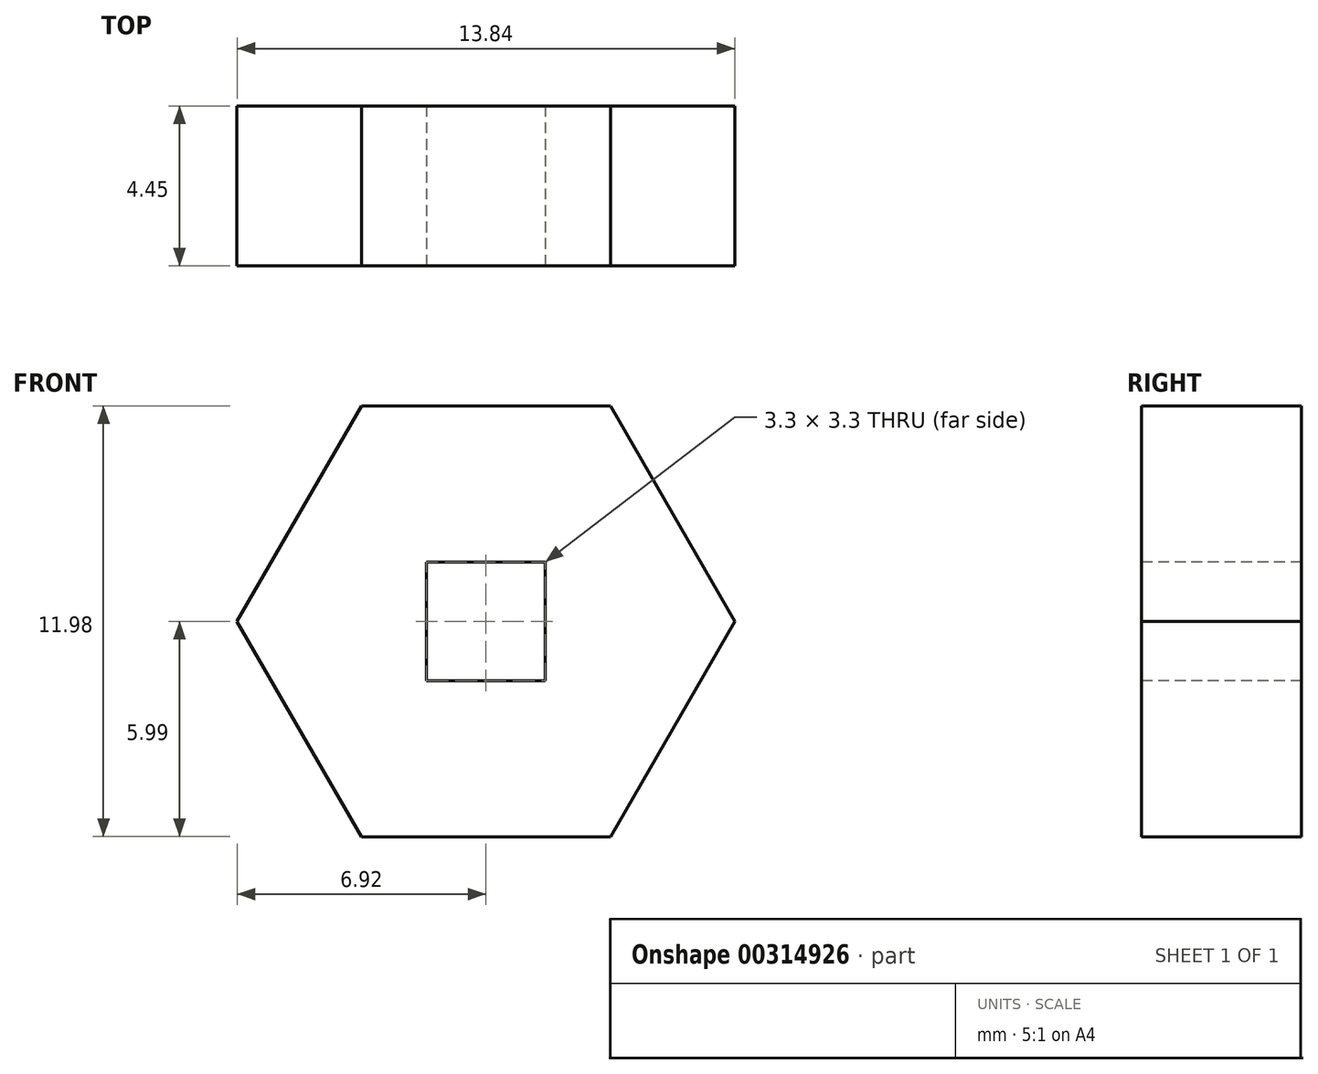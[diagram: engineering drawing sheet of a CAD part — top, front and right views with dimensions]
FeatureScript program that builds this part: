
annotation { "Feature Type Name" : "Feature", "Feature Type Description" : "" }
export const myFeature = defineFeature(function(context is Context, id is Id, definition is map)
    precondition{}
    {
        {
            var Q0;
            Q0=qCreatedBy(makeId("Front.planeOp"),FACE);
            var sketch = newSketch(context, id + "F0", { "sketchPlane" : qUnion([Q0])});
            skCircle(sketch, "E0.cCircle", {"center": v(0, 0) * mm, "radius": 6 * mm, "construction": true});
            skLineSegment(sketch, "E0.0", {"start": v(-3.46, 6) * mm, "end": v(3.46, 6) * mm});
            skLineSegment(sketch, "E0.1", {"start": v(3.46, 6) * mm, "end": v(6.92, 0) * mm});
            skLineSegment(sketch, "E0.2", {"start": v(6.92, 0) * mm, "end": v(3.46, -6) * mm});
            skLineSegment(sketch, "E0.3", {"start": v(3.46, -6) * mm, "end": v(-3.46, -6) * mm});
            skLineSegment(sketch, "E0.4", {"start": v(-3.46, -6) * mm, "end": v(-6.92, 0) * mm});
            skLineSegment(sketch, "E0.5", {"start": v(-6.92, 0) * mm, "end": v(-3.46, 6) * mm});
            skPoint(sketch, "E0.0.midPoint", {"position": v(0, 6) * mm});
            skSolve(sketch);
        }
        {
            var Q0;
            Q0=makeQuery(id+"F0.imprint","IMPRINT",FACE,{"disambiguationData":[TD([[makeQuery(id+"F0.imprint","IMPRINT",EDGE,{"derivedFrom":sQuery(id+"F0.wireOp",EDGE,"E0.0")}),-1.0]])]});
            extrude(context, id + "F1", {"entities" : qUnion([Q0]), "depth" : 4.44 * mm});
        }
        {
            var Q0;
            Q0=makeQuery(id+"F1.opExtrude","CAP_FACE",FACE,{"disambiguationData":[OSD([sQuery(id+"F0.wireOp",EDGE,"E0.0"),sQuery(id+"F0.wireOp",EDGE,"E0.1"),sQuery(id+"F0.wireOp",EDGE,"E0.2"),sQuery(id+"F0.wireOp",EDGE,"E0.3"),sQuery(id+"F0.wireOp",EDGE,"E0.4"),sQuery(id+"F0.wireOp",EDGE,"E0.5")])],"isStart":false});
            var sketch = newSketch(context, id + "F2", { "sketchPlane" : qUnion([Q0])});
            skLineSegment(sketch, "E1.bottom", {"start": v(1.65, 1.65) * mm, "end": v(-1.65, 1.65) * mm});
            skLineSegment(sketch, "E1.top", {"start": v(1.65, -1.65) * mm, "end": v(-1.65, -1.65) * mm});
            skLineSegment(sketch, "E1.left", {"start": v(1.65, 1.65) * mm, "end": v(1.65, -1.65) * mm});
            skLineSegment(sketch, "E1.right", {"start": v(-1.65, 1.65) * mm, "end": v(-1.65, -1.65) * mm});
            skPoint(sketch, "E1.middle", {"position": v(0, 0) * mm});
            skSolve(sketch);
        }
        {
            var Q0;
            Q0=makeQuery(id+"F2.imprint","IMPRINT",FACE,{"disambiguationData":[TD([[makeQuery(id+"F2.imprint","IMPRINT",EDGE,{"derivedFrom":sQuery(id+"F2.wireOp",EDGE,"E1.bottom")}),1.0]])]});
            extrude(context, id + "F3", {"entities" : qUnion([Q0]), "operationType" : NewBodyOperationType.REMOVE, "oppositeDirection" : true, "depth" : 25.4 * mm});
        }
    });
